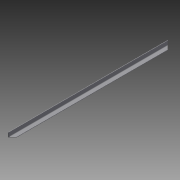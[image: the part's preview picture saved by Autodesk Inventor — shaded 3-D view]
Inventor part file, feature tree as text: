
AUTODESK INVENTOR PART (.ipt)
format: ipt  version: 2014 (Build 180170000, 170)  size: 94,208 bytes
history: native  units: in
note: dims shown in document units (in); Inventor stores cm internally (conversion verified against a paired STEP export)
features: extrude x3, sketch x3
ambient origin geometry x8: Origin, YZ Plane, XZ Plane, XY Plane, X Axis, Y Axis, Z Axis, Center Point
bodies: Solid1 (feature_tree)
feature tree (6):
  extrude  "angle"  Depth=1.0in
  extrude  "ends"  Depth=0.125in
  extrude  "Extrusion3"  TaperAngle=45.0deg  [1 undecoded]
  sketch  "Sketch1"  dims[d0=1.0in d1=1.0in]
  sketch  "Sketch2"  dims[d2=0.1in d3=0.125in]
  sketch  "Sketch3"  dims[d4=36.2in d5=0.0in d6=45.0deg d7=45.0deg d8=36.0in d9=0.0in d10=0.1in d11=0.0in]
note: 1 required parameter value undecoded (feature->parameter linkage not recoverable at this tier; creation-order binding heuristic only, values carry confidence <= 0.55)
